# Revit family: Legrand Caja Plexo³ 4-8 módulos
name_source: partatom
category: Equipement électrique
revit_build: Autodesk Revit 2018 (Build: 20170223_1515(x64)
units: mm (PartAtom-declared; Revit-internal decimal feet)

## family parameters
Basée sur le plan de construction = Non
Configuration du panneau = Deux colonnes, circuits au sein
Cote de connecteur circulaire = Utiliser le diamètre
Couper avec des vides une fois chargée = Non
Numéro OmniClass = 23.80.30.11.17
Partagée = Non
Point de calcul de pièce = Non
Titre OmniClass = Distribution Boards and Control Panels
Toujours verticalement = Oui
Type d'élément = Tableau de raccordement

## types (13) — shared parameters
Condiciones Generales de Uso = https://export.legrand.com
ETIM Class 6.0 = EC000214
Fabricant = Legrand
IK = 09
IP = 65
Materia = Poliestireno
RAL = 7046
URL = www.legrand.fr

## per-type parameters (varying)
| type | Bornas N | Bornas T | Caja 001904 | Caja 001906 | Caja 001908 | Caja 601954 | Caja 601956 | Caja 601958 | Caja 601974 | Caja 601976 | Caja 601978 | Caja 601994 | Caja 601996 | Caja 601998 | Description | Image du type |
| Plexo³ 4 módulos de 1 fila  001904 |  |  | Oui | Non | Non | Non | Non | Non | Non | Non | Non | Non | Non | Non | Plexo³ 4 módulos de 1 fila  001904 | plexo3_6modules_001906_pw_182611_pz_4.jpg |
| Plexo³ 6 módulos de 1 fila  001906 |  | terminal 1+6 hoyos | Non | Oui | Non | Non | Non | Non | Non | Non | Non | Non | Non | Non | Plexo³ 6 módulos de 1 fila  001906 | plexo3_6modules_001906_pw_182611_pz_4.jpg |
| Plexo³ 8 módulos de 1 fila  001908 |  | terminal 1+6 hoyos | Non | Non | Oui | Non | Non | Non | Non | Non | Non | Non | Non | Non | Plexo³ 8 módulos de 1 fila  001908 | <Aucun> |
| Plexo³ 4 módulos de 1 fila  601954 |  |  | Non | Non | Non | Oui | Non | Non | Non | Non | Non | Non | Non | Non | Plexo³ 4 módulos de 1 fila  601954 | plexo3_6modules_001906_pw_182611_pz_4.jpg |
| Plexo³ 4 módulos de 1 fila  601974 | terminal 4 hoyos | terminal 4 hoyos | Non | Non | Non | Non | Non | Non | Oui | Non | Non | Non | Non | Non | Plexo³ 4 módulos de 1 fila  601974 | plexo3_6modules_001906_pw_182611_pz_4.jpg |
| Plexo³ 4 módulos de 1 fila  601996 |  |  | Non | Non | Non | Non | Non | Non | Non | Non | Non | Non | Oui | Non | Plexo³ 4 módulos de 1 fila  601996 | plexo3_6modules_001906_pw_182611_pz_4.jpg |
| Plexo³ 6 módulos de 1 fila  601956 |  |  | Non | Non | Non | Non | Oui | Non | Non | Non | Non | Non | Non | Non | Plexo³ 6 módulos de 1 fila  601956 | plexo3_6modules_001906_pw_182611_pz_4.jpg |
| Plexo³ 6 módulos de 1 fila  601976 | terminal 4 hoyos | terminal 4 hoyos | Non | Non | Non | Non | Non | Non | Non | Oui | Non | Non | Non | Non | Plexo³ 6 módulos de 1 fila  601976 | plexo3_6modules_001906_pw_182611_pz_4.jpg |
| Plexo³ 8 módulos de 1 fila  601958 |  |  | Non | Non | Non | Non | Non | Oui | Non | Non | Non | Non | Non | Non | Plexo³ 8 módulos de 1 fila  601958 | <Aucun> |
| Plexo³ 8 módulos de 1 fila  601978 | terminal 8 hoyos | terminal 8 hoyos | Non | Non | Non | Non | Non | Non | Non | Non | Oui | Non | Non | Non | Plexo³ 8 módulos de 1 fila  601978 | <Aucun> |
| Plexo³ 8 módulos de 1 fila  601998 | terminal 8 hoyos | terminal 8 hoyos | Non | Non | Non | Non | Non | Non | Non | Non | Non | Non | Non | Oui | Plexo³ 8 módulos de 1 fila  601978 | <Aucun> |
| Plexo³ 8 módulos de 1 fila  601996 | terminal 8 hoyos | terminal 8 hoyos | Non | Non | Non | Non | Non | Non | Non | Non | Non | Non | Oui | Non | Plexo³ 6 módulos de 1 fila  601996 | <Aucun> |
| Plexo³ 8 módulos de 1 fila  601994 | terminal 8 hoyos | terminal 8 hoyos | Non | Non | Non | Non | Non | Non | Non | Non | Non | Oui | Non | Non | Plexo³ 4 módulos de 1 fila  601994 | <Aucun> |
